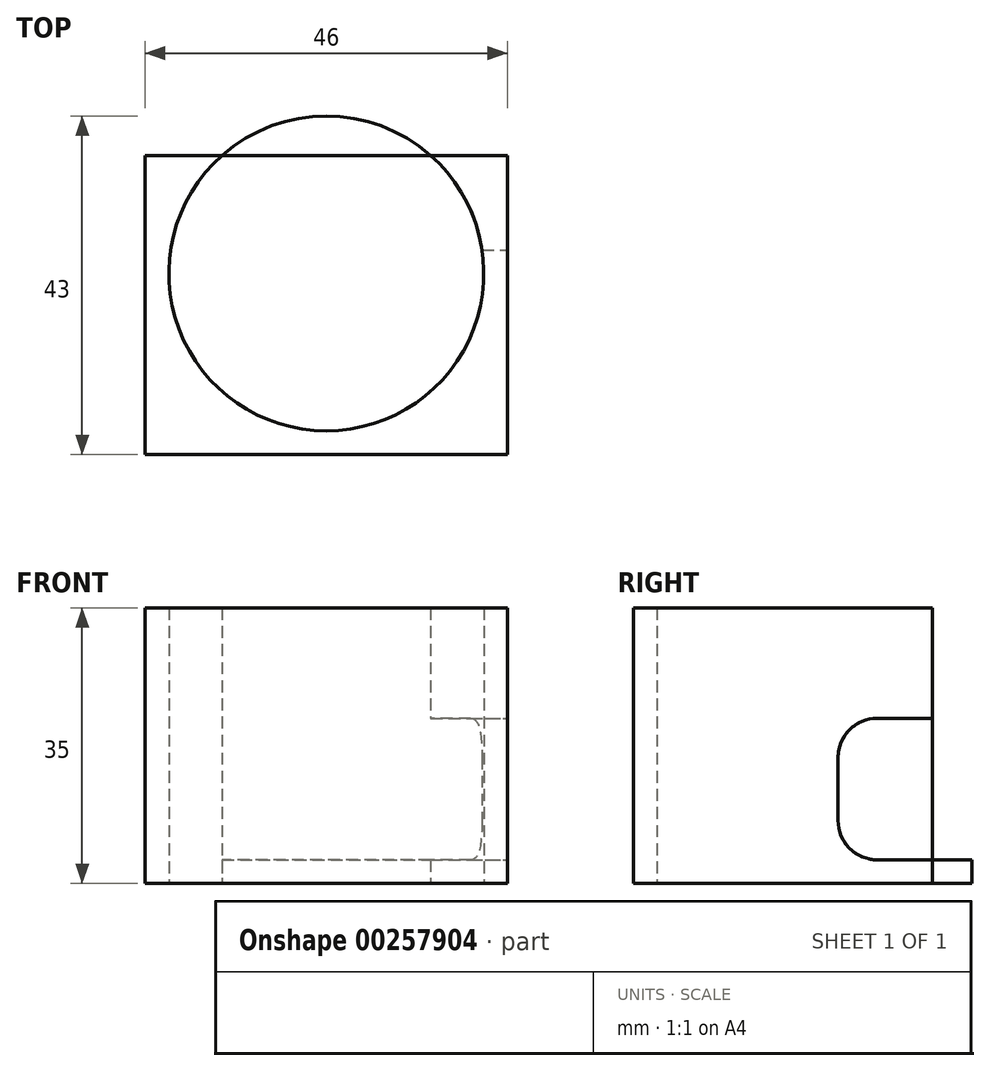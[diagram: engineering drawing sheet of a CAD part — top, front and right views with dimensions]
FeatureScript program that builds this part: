
annotation { "Feature Type Name" : "Feature", "Feature Type Description" : "" }
export const myFeature = defineFeature(function(context is Context, id is Id, definition is map)
    precondition{}
    {
        {
            var Q0;
            Q0=qCreatedBy(makeId("Top.planeOp"),FACE);
            var sketch = newSketch(context, id + "F0", { "sketchPlane" : qUnion([Q0])});
            skLineSegment(sketch, "E0.bottom", {"start": v(-23, 23) * mm, "end": v(23, 23) * mm});
            skLineSegment(sketch, "E0.top", {"start": v(-23, -23) * mm, "end": v(23, -23) * mm});
            skLineSegment(sketch, "E0.left", {"start": v(-23, 23) * mm, "end": v(-23, -23) * mm});
            skLineSegment(sketch, "E0.right", {"start": v(23, 23) * mm, "end": v(23, -23) * mm});
            skCircle(sketch, "E1", {"center": v(0, 0) * mm, "radius": 20 * mm});
            skLineSegment(sketch, "E2", {"start": v(-23, 15) * mm, "end": v(23, 15) * mm});
            skSolve(sketch);
        }
        {
            var Q0;
            {var subQ5=sQuery(id+"F0.wireOp",EDGE,"E0.top");Q0=makeQuery(id+"F0.imprint","IMPRINT",FACE,{"disambiguationData":[TD([[makeQuery(id+"F0.imprint","IMPRINT",EDGE,{"derivedFrom":subQ5}),1.0]])]});}
            extrude(context, id + "F1", {"entities" : qUnion([Q0]), "depth" : 35 * mm});
        }
        {
            var Q0;
            {var subQ0=sQuery(id+"F0.wireOp",EDGE,"E2");var subQ1=sQuery(id+"F0.wireOp",EDGE,"E1");var subQ2=makeQuery(id+"F0.imprint","INTERSECT",VERTEX,{"disambiguationData":[OD(0.0)],"derivedFrom":[subQ1,subQ0]});Q0=makeQuery(id+"F0.imprint","IMPRINT",FACE,{"disambiguationData":[TD([[makeQuery(id+"F0.imprint","IMPRINT",EDGE,{"disambiguationData":[TD([[subQ2,-1.0]])],"derivedFrom":subQ1}),1.0]])]});}
            extrude(context, id + "F2", {"entities" : qUnion([Q0]), "operationType" : NewBodyOperationType.ADD, "depth" : 3 * mm});
        }
        {
            var Q0;
            {var subQ0=sQuery(id+"F0.wireOp",EDGE,"E2");Q0=makeQuery(id+"F2.boolean.opBoolean","MERGE",FACE,{"derivedFrom":[makeQuery(id+"F1.opExtrude","SWEPT_FACE",FACE,{"disambiguationData":[OSD([subQ0]),TDD([makeQuery(id+"F0.imprint","IMPRINT",EDGE,{"disambiguationData":[TD([[makeQuery(id+"F0.imprint","INTERSECT",VERTEX,{"derivedFrom":[sQuery(id+"F0.wireOp",EDGE,"E0.left"),subQ0]}),-1.0]])],"derivedFrom":subQ0})])]}),makeQuery(id+"F1.opExtrude","SWEPT_FACE",FACE,{"disambiguationData":[OSD([subQ0]),TDD([makeQuery(id+"F0.imprint","IMPRINT",EDGE,{"disambiguationData":[TD([[makeQuery(id+"F0.imprint","INTERSECT",VERTEX,{"derivedFrom":[sQuery(id+"F0.wireOp",EDGE,"E0.right"),subQ0]}),1.0]])],"derivedFrom":subQ0})])]}),makeQuery(id+"F2.opExtrude","SWEPT_FACE",FACE,{"disambiguationData":[OSD([subQ0])]})]});}
            var sketch = newSketch(context, id + "F3", { "sketchPlane" : qUnion([Q0])});
            skLineSegment(sketch, "E3.bottom", {"start": v(-13.23, 3) * mm, "end": v(-23, 3) * mm});
            skLineSegment(sketch, "E3.top", {"start": v(-13.23, 21) * mm, "end": v(-23, 21) * mm});
            skLineSegment(sketch, "E3.left", {"start": v(-13.23, 3) * mm, "end": v(-13.23, 21) * mm});
            skLineSegment(sketch, "E3.right", {"start": v(-23, 3) * mm, "end": v(-23, 21) * mm});
            skSolve(sketch);
        }
        {
            var Q0;
            Q0 = qSketchRegion(id + "F3", true);
            extrude(context, id + "F4", {"entities" : qUnion([Q0]), "operationType" : NewBodyOperationType.REMOVE, "oppositeDirection" : true, "depth" : 12 * mm});
        }
        {
            var Q0;
            Q0=makeQuery(id+"F4.boolean.opBoolean","COPY",EDGE,{"derivedFrom":makeQuery(id+"F4.opExtrude","CAP_EDGE",EDGE,{"disambiguationData":[OSD([sQuery(id+"F3.wireOp",EDGE,"E3.top")])],"isStart":false})});
            var Q1;
            Q1=makeQuery(id+"F4.boolean.opBoolean","COPY",EDGE,{"derivedFrom":makeQuery(id+"F4.opExtrude","CAP_EDGE",EDGE,{"disambiguationData":[OSD([sQuery(id+"F3.wireOp",EDGE,"E3.bottom")])],"isStart":false})});
            fillet(context, id + "F5", {"entities" : qUnion([Q0, Q1]), "radius" : 5 * mm, "tangentPropagation" : true, "allowEdgeOverflow" : false});
        }
    });
